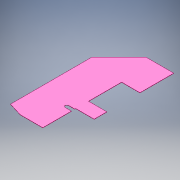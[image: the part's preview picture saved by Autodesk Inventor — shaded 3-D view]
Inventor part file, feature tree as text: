
AUTODESK INVENTOR PART (.ipt)
format: ipt  version: 2018 (Build 220112000, 112)  size: 154,624 bytes
history: native  units: mm
features: extrude x1, sketch x1
ambient origin geometry x8: Origin, YZ Plane, XZ Plane, XY Plane, X Axis, Y Axis, Z Axis, Center Point
bodies: Solid1 (feature_tree)
feature tree (2):
  extrude  "Extrusion1"  Depth=235.0mm
  sketch  "Sketch1"  dims[d0=159.0mm d3=100.0mm d6=800.0mm d7=240.0mm d8=130.0mm d11=235.0mm d12=1.6mm d13=0.0mm d14=25.0mm d16=216.0mm d17=0.0mm d18=45.0mm d19=389.0mm d22=130.0mm d23=235.0mm d25=30.0mm d26=270.0mm d27=135.0deg]
